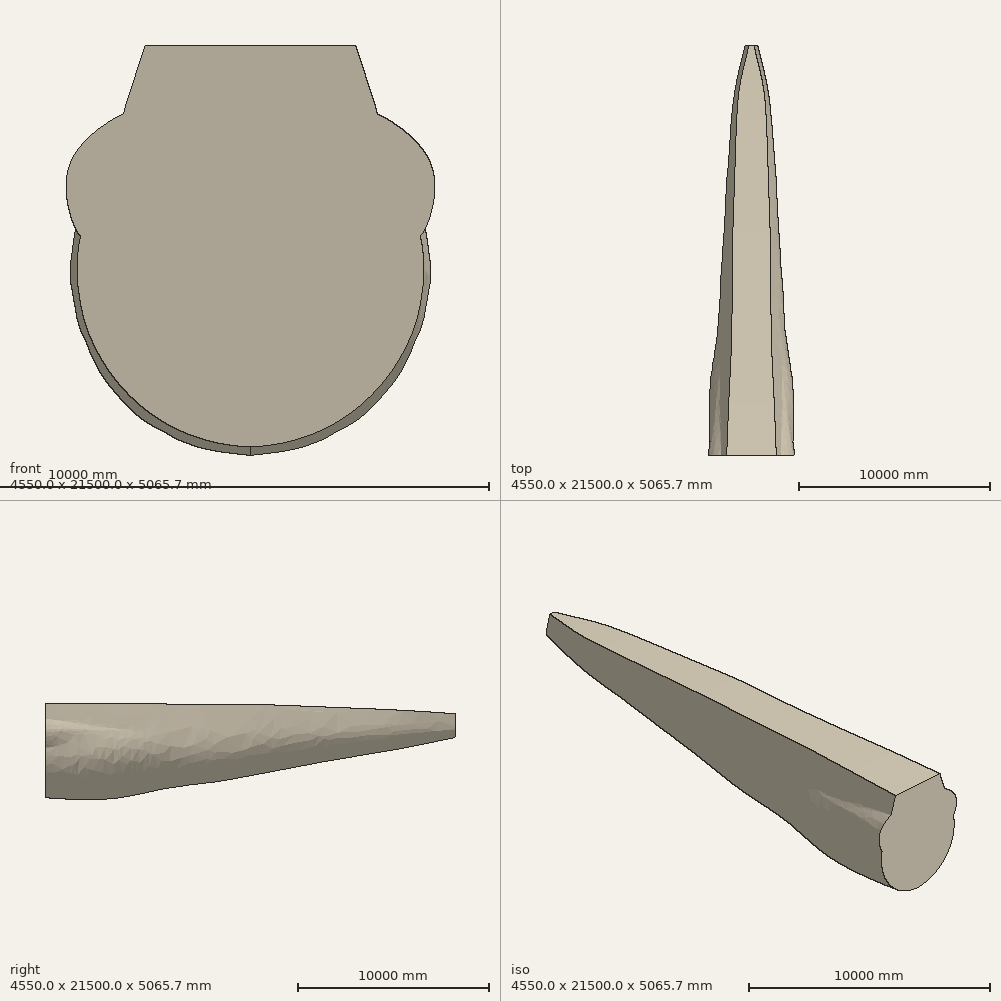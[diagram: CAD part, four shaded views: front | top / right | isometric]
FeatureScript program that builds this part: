
annotation { "Feature Type Name" : "Feature", "Feature Type Description" : "" }
export const myFeature = defineFeature(function(context is Context, id is Id, definition is map)
    precondition{}
    {
        {
            var Q0;
            Q0=qCreatedBy(makeId("Front.planeOp"),FACE);
            var sketch = newSketch(context, id + "F0", { "sketchPlane" : qUnion([Q0])});
            skLineSegment(sketch, "E0", {"start": v(0, 957.5) * mm, "end": v(0, -6184.63) * mm, "construction": true});
            skSolve(sketch);
        }
        {
            var Q0;
            Q0=qCreatedBy(makeId("Front.planeOp"),FACE);
            cPlane(context, id + "F1", {"entities" : qUnion([Q0]), "cplaneType" : CPlaneType.OFFSET, "offset" : 15 * 500 * mm, "oppositeDirection" : true, "width" : 150 * mm, "height" : 150 * mm});
        }
        {
            var Q0;
            Q0=qCreatedBy(id+"F1.planeOp",FACE);
            var sketch = newSketch(context, id + "F2", { "sketchPlane" : qUnion([Q0])});
            skLineSegment(sketch, "E1", {"start": v(0, -542.73) * mm, "end": v(127.4, -542.73) * mm});
            skFitSpline(sketch, "E2", {"points": [v(127.4, -542.73) * mm, v(327.33, -1279.15) * mm, v(301.38, -1495.38) * mm, v(0, -1799.57) * mm], "startDerivative": vector(509.68, -1641.96) * mm, "endDerivative": vector(-1468.27, -1174.11) * mm});
            skLineSegment(sketch, "E3", {"start": v(0, -262.95) * mm, "end": v(0, -1902.41) * mm, "construction": true});
            skLineSegment(sketch, "E4.MirrorCS", {"start": v(0, -542.73) * mm, "end": v(-127.4, -542.73) * mm});
            skFitSpline(sketch, "E5.MirrorCS", {"points": [v(-127.4, -542.73) * mm, v(-327.33, -1279.15) * mm, v(-301.38, -1495.38) * mm, v(0, -1799.57) * mm], "startDerivative": vector(-509.68, -1641.96) * mm, "endDerivative": vector(1468.27, -1174.11) * mm});
            skSolve(sketch);
        }
        {
            var Q0;
            Q0=qCreatedBy(makeId("Front.planeOp"),FACE);
            cPlane(context, id + "F3", {"entities" : qUnion([Q0]), "cplaneType" : CPlaneType.OFFSET, "offset" : 5000 * mm, "oppositeDirection" : true, "width" : 150 * mm, "height" : 150 * mm});
        }
        {
            var Q0;
            Q0=qCreatedBy(id+"F3.planeOp",FACE);
            var sketch = newSketch(context, id + "F4", { "sketchPlane" : qUnion([Q0])});
            skLineSegment(sketch, "E6", {"start": v(0, -378.18) * mm, "end": v(673.11, -378.18) * mm});
            skFitSpline(sketch, "E7", {"points": [v(673.11, -378.18) * mm, v(880.4, -1250.97) * mm, v(804.03, -1789.18) * mm, v(0, -2312.85) * mm], "startDerivative": vector(865.3, -3518.16) * mm, "endDerivative": vector(-3263.23, -945.44) * mm});
            skLineSegment(sketch, "E8.MirrorCS", {"start": v(0, -378.18) * mm, "end": v(-673.11, -378.18) * mm});
            skFitSpline(sketch, "E9.MirrorCS", {"points": [v(-673.11, -378.18) * mm, v(-880.4, -1250.97) * mm, v(-804.03, -1789.18) * mm, v(0, -2312.85) * mm], "startDerivative": vector(-865.3, -3518.16) * mm, "endDerivative": vector(3263.23, -945.44) * mm});
            skSolve(sketch);
        }
        {
            var Q0;
            Q0=qCreatedBy(makeId("Front.planeOp"),FACE);
            cPlane(context, id + "F5", {"entities" : qUnion([Q0]), "cplaneType" : CPlaneType.OFFSET, "offset" : 2500 * mm, "oppositeDirection" : true, "width" : 150 * mm, "height" : 150 * mm});
        }
        {
            var Q0;
            Q0=qCreatedBy(id+"F5.planeOp",FACE);
            var sketch = newSketch(context, id + "F6", { "sketchPlane" : qUnion([Q0])});
            skLineSegment(sketch, "E10", {"start": v(0, -260.03) * mm, "end": v(815.73, -260.03) * mm});
            skFitSpline(sketch, "E11", {"points": [v(815.73, -260.03) * mm, v(1139.68, -1511.37) * mm, v(945.64, -2183.08) * mm, v(0, -2720.38) * mm], "startDerivative": vector(1362.63, -4474.69) * mm, "endDerivative": vector(-3636.02, -596.27) * mm});
            skLineSegment(sketch, "E12.MirrorCS", {"start": v(0, -260.03) * mm, "end": v(-815.73, -260.03) * mm});
            skFitSpline(sketch, "E13.MirrorCS", {"points": [v(-815.73, -260.03) * mm, v(-1139.68, -1511.37) * mm, v(-945.64, -2183.08) * mm, v(0, -2720.38) * mm], "startDerivative": vector(-1362.63, -4474.69) * mm, "endDerivative": vector(3636.02, -596.27) * mm});
            skSolve(sketch);
        }
        {
            var Q0;
            Q0=qCreatedBy(makeId("Front.planeOp"),FACE);
            var sketch = newSketch(context, id + "F7", { "sketchPlane" : qUnion([Q0])});
            skLineSegment(sketch, "E14", {"start": v(0, -157.38) * mm, "end": v(-918.22, -157.38) * mm});
            skFitSpline(sketch, "E15", {"points": [v(-918.22, -157.38) * mm, v(-1147.06, -903.22) * mm, v(-1325.56, -1802.54) * mm, v(-958.25, -2698.42) * mm, v(0, -3175.48) * mm], "startDerivative": vector(-1286.95, -3604.77) * mm, "endDerivative": vector(4961.26, -806.09) * mm});
            skLineSegment(sketch, "E16.MirrorCS", {"start": v(0, -157.38) * mm, "end": v(918.22, -157.38) * mm});
            skFitSpline(sketch, "E17.MirrorCS", {"points": [v(918.22, -157.38) * mm, v(1147.06, -903.22) * mm, v(1325.56, -1802.54) * mm, v(958.25, -2698.42) * mm, v(0, -3175.48) * mm], "startDerivative": vector(1286.95, -3604.77) * mm, "endDerivative": vector(-4961.26, -806.09) * mm});
            skSolve(sketch);
        }
        {
            var Q0;
            Q0=qCreatedBy(makeId("Front.planeOp"),FACE);
            cPlane(context, id + "F8", {"entities" : qUnion([Q0]), "cplaneType" : CPlaneType.OFFSET, "offset" : 2500 * mm, "width" : 150 * mm, "height" : 150 * mm});
        }
        {
            var Q0;
            Q0=qCreatedBy(id+"F8.planeOp",FACE);
            var sketch = newSketch(context, id + "F9", { "sketchPlane" : qUnion([Q0])});
            skLineSegment(sketch, "E18", {"start": v(0, -68) * mm, "end": v(-982.64, -68) * mm});
            skFitSpline(sketch, "E19", {"points": [v(-982.64, -68) * mm, v(-1440.02, -2273.66) * mm, v(-822.17, -3354.9) * mm, v(0, -3638.79) * mm], "startDerivative": vector(-2027.04, -7338.74) * mm, "endDerivative": vector(2887.52, 11.21) * mm});
            skLineSegment(sketch, "E20.MirrorCS", {"start": v(0, -68) * mm, "end": v(982.64, -68) * mm});
            skFitSpline(sketch, "E21.MirrorCS", {"points": [v(982.64, -68) * mm, v(1440.02, -2273.66) * mm, v(822.17, -3354.9) * mm, v(0, -3638.79) * mm], "startDerivative": vector(2027.04, -7338.74) * mm, "endDerivative": vector(-2887.52, 11.21) * mm});
            skSolve(sketch);
        }
        {
            var Q0;
            Q0=qCreatedBy(makeId("Front.planeOp"),FACE);
            cPlane(context, id + "F10", {"entities" : qUnion([Q0]), "cplaneType" : CPlaneType.OFFSET, "offset" : 5000 * mm, "width" : 150 * mm, "height" : 150 * mm});
        }
        {
            var Q0;
            Q0=qCreatedBy(id+"F10.planeOp",FACE);
            var sketch = newSketch(context, id + "F11", { "sketchPlane" : qUnion([Q0])});
            skLineSegment(sketch, "E22", {"start": v(0, -68.8) * mm, "end": v(-1006.51, -68.8) * mm});
            skFitSpline(sketch, "E23", {"points": [v(-1006.51, -68.8) * mm, v(-1628.37, -2323.5) * mm, v(-1177.43, -3585.4) * mm, v(0, -4109.07) * mm], "startDerivative": vector(-1881.34, -6080.27) * mm, "endDerivative": vector(4120.28, 36.86) * mm});
            skLineSegment(sketch, "E24.MirrorCS", {"start": v(0, -68.8) * mm, "end": v(1006.51, -68.8) * mm});
            skFitSpline(sketch, "E25.MirrorCS", {"points": [v(1006.51, -68.8) * mm, v(1628.37, -2323.5) * mm, v(1177.43, -3585.4) * mm, v(0, -4109.07) * mm], "startDerivative": vector(1881.34, -6080.27) * mm, "endDerivative": vector(-4120.28, 36.86) * mm});
            skSolve(sketch);
        }
        {
            var Q0;
            Q0=qCreatedBy(makeId("Front.planeOp"),FACE);
            cPlane(context, id + "F12", {"entities" : qUnion([Q0]), "cplaneType" : CPlaneType.OFFSET, "offset" : 7500 * mm, "width" : 150 * mm, "height" : 150 * mm});
        }
        {
            var Q0;
            Q0=qCreatedBy(id+"F12.planeOp",FACE);
            var sketch = newSketch(context, id + "F13", { "sketchPlane" : qUnion([Q0])});
            skLineSegment(sketch, "E26", {"start": v(0, -35.47) * mm, "end": v(-1022.58, -35.47) * mm});
            skFitSpline(sketch, "E27", {"points": [v(-1022.58, -35.47) * mm, v(-1495.4, -1322.73) * mm, v(-1781.8, -2550.86) * mm, v(-1223.56, -3910.06) * mm, v(0, -4429.47) * mm], "startDerivative": vector(-3277.87, -8626.85) * mm, "endDerivative": vector(3887.58, -58.84) * mm});
            skLineSegment(sketch, "E28.MirrorCS", {"start": v(0, -35.47) * mm, "end": v(1022.58, -35.47) * mm});
            skFitSpline(sketch, "E29.MirrorCS", {"points": [v(1022.58, -35.47) * mm, v(1495.4, -1322.73) * mm, v(1781.8, -2550.86) * mm, v(1223.56, -3910.06) * mm, v(0, -4429.47) * mm], "startDerivative": vector(3277.87, -8626.85) * mm, "endDerivative": vector(-3887.58, -58.84) * mm});
            skSolve(sketch);
        }
        {
            var Q0;
            Q0=qCreatedBy(makeId("Front.planeOp"),FACE);
            cPlane(context, id + "F14", {"entities" : qUnion([Q0]), "cplaneType" : CPlaneType.OFFSET, "offset" : 10000 * mm, "width" : 150 * mm, "height" : 150 * mm});
        }
        {
            var Q0;
            Q0=qCreatedBy(id+"F14.planeOp",FACE);
            var sketch = newSketch(context, id + "F15", { "sketchPlane" : qUnion([Q0])});
            skLineSegment(sketch, "E30", {"start": v(0, 0) * mm, "end": v(1135.79, 0) * mm});
            skFitSpline(sketch, "E31", {"points": [v(1135.79, 0) * mm, v(1590.03, -1256.67) * mm, v(1636.2, -1382.8) * mm, v(1688.85, -1442.46) * mm, v(2127.52, -2519.85) * mm, v(1446.9, -4372.15) * mm, v(0, -4942.68) * mm], "startDerivative": vector(3324.53, -8985.96) * mm, "endDerivative": vector(-6038.72, -251.6) * mm});
            skLineSegment(sketch, "E32.MirrorCS", {"start": v(0, 0) * mm, "end": v(-1135.79, 0) * mm});
            skLineSegment(sketch, "E33.MirrorCS", {"start": v(-1135.79, 0) * mm, "end": v(-1135.79, 0) * mm});
            skFitSpline(sketch, "E34.MirrorCS", {"points": [v(-1135.79, 0) * mm, v(-1590.03, -1256.67) * mm, v(-1636.2, -1382.8) * mm, v(-1688.85, -1442.46) * mm, v(-2127.52, -2519.85) * mm, v(-1446.9, -4372.15) * mm, v(0, -4942.68) * mm], "startDerivative": vector(-3324.53, -8985.96) * mm, "endDerivative": vector(6038.72, -251.6) * mm});
            skSolve(sketch);
        }
        {
            var Q0;
            Q0=qCreatedBy(makeId("Front.planeOp"),FACE);
            cPlane(context, id + "F16", {"entities" : qUnion([Q0]), "cplaneType" : CPlaneType.OFFSET, "offset" : 14000 * mm, "width" : 150 * mm, "height" : 150 * mm});
        }
        {
            var Q0;
            Q0=qCreatedBy(id+"F16.planeOp",FACE);
            var sketch = newSketch(context, id + "F17", { "sketchPlane" : qUnion([Q0])});
            skLineSegment(sketch, "E35", {"start": v(0, 0) * mm, "end": v(1301.27, 0) * mm});
            skFitSpline(sketch, "E36", {"points": [v(1301.27, 0) * mm, v(1553.7, -790.28) * mm, v(1568.6, -839.96) * mm, v(1623.26, -868.12) * mm, v(2232.1, -1470.35) * mm, v(2138.92, -2295.56) * mm, v(2102.48, -2347.56) * mm, v(2117.98, -2453.36) * mm, v(2067.99, -3325.79) * mm, v(1299.73, -4487.54) * mm, v(0, -4947.93) * mm], "startDerivative": vector(2597.56, -7814.52) * mm, "endDerivative": vector(-8634.71, -306.24) * mm});
            skLineSegment(sketch, "E37.MirrorCS", {"start": v(0, 0) * mm, "end": v(-1301.27, 0) * mm});
            skFitSpline(sketch, "E38.MirrorCS", {"points": [v(-1301.27, 0) * mm, v(-1553.7, -790.28) * mm, v(-1568.6, -839.96) * mm, v(-1623.26, -868.12) * mm, v(-2232.1, -1470.35) * mm, v(-2138.92, -2295.56) * mm, v(-2102.48, -2347.56) * mm, v(-2117.98, -2453.36) * mm, v(-2067.99, -3325.79) * mm, v(-1299.73, -4487.54) * mm, v(0, -4947.93) * mm], "startDerivative": vector(-2597.56, -7814.52) * mm, "endDerivative": vector(8634.71, -306.24) * mm});
            skSolve(sketch);
        }
        {
            var Q0;
            Q0=qCreatedBy(makeId("Front.planeOp"),FACE);
            cPlane(context, id + "F18", {"entities" : qUnion([Q0]), "cplaneType" : CPlaneType.OFFSET, "offset" : 24500 * mm, "width" : 150 * mm, "height" : 150 * mm});
        }
        {
            var Q0;
            Q0=makeQuery(id+"F2.imprint","IMPRINT",FACE,{"disambiguationData":[TD([[makeQuery(id+"F2.imprint","IMPRINT",EDGE,{"derivedFrom":sQuery(id+"F2.wireOp",EDGE,"E1")}),-1.0]])]});
            var Q1;
            Q1=makeQuery(id+"F4.imprint","IMPRINT",FACE,{"disambiguationData":[TD([[makeQuery(id+"F4.imprint","IMPRINT",EDGE,{"derivedFrom":sQuery(id+"F4.wireOp",EDGE,"E6")}),-1.0]])]});
            var Q2;
            Q2=makeQuery(id+"F6.imprint","IMPRINT",FACE,{"disambiguationData":[TD([[makeQuery(id+"F6.imprint","IMPRINT",EDGE,{"derivedFrom":sQuery(id+"F6.wireOp",EDGE,"E10")}),-1.0]])]});
            var Q3;
            Q3=makeQuery(id+"F7.imprint","IMPRINT",FACE,{"disambiguationData":[TD([[makeQuery(id+"F7.imprint","IMPRINT",EDGE,{"derivedFrom":sQuery(id+"F7.wireOp",EDGE,"E14")}),1.0]])]});
            var Q4;
            Q4=makeQuery(id+"F9.imprint","IMPRINT",FACE,{"disambiguationData":[TD([[makeQuery(id+"F9.imprint","IMPRINT",EDGE,{"derivedFrom":sQuery(id+"F9.wireOp",EDGE,"E18")}),1.0]])]});
            var Q5;
            Q5=makeQuery(id+"F11.imprint","IMPRINT",FACE,{"disambiguationData":[TD([[makeQuery(id+"F11.imprint","IMPRINT",EDGE,{"derivedFrom":sQuery(id+"F11.wireOp",EDGE,"E22")}),1.0]])]});
            var Q6;
            Q6=makeQuery(id+"F13.imprint","IMPRINT",FACE,{"disambiguationData":[TD([[makeQuery(id+"F13.imprint","IMPRINT",EDGE,{"derivedFrom":sQuery(id+"F13.wireOp",EDGE,"E26")}),1.0]])]});
            var Q7;
            Q7=makeQuery(id+"F15.imprint","IMPRINT",FACE,{"disambiguationData":[TD([[makeQuery(id+"F15.imprint","IMPRINT",EDGE,{"derivedFrom":sQuery(id+"F15.wireOp",EDGE,"E30")}),-1.0]])]});
            var Q8;
            Q8=makeQuery(id+"F17.imprint","IMPRINT",FACE,{"disambiguationData":[TD([[makeQuery(id+"F17.imprint","IMPRINT",EDGE,{"derivedFrom":sQuery(id+"F17.wireOp",EDGE,"E35")}),-1.0]])]});
            loft(context, id + "F19", {"sheetProfilesArray" : [{ "sheetProfileEntities" : qUnion([Q0]) }, { "sheetProfileEntities" : qUnion([Q1]) }, { "sheetProfileEntities" : qUnion([Q2]) }, { "sheetProfileEntities" : qUnion([Q3]) }, { "sheetProfileEntities" : qUnion([Q4]) }, { "sheetProfileEntities" : qUnion([Q5]) }, { "sheetProfileEntities" : qUnion([Q6]) }, { "sheetProfileEntities" : qUnion([Q7]) }, { "sheetProfileEntities" : qUnion([Q8]) }]});
        }
    });
